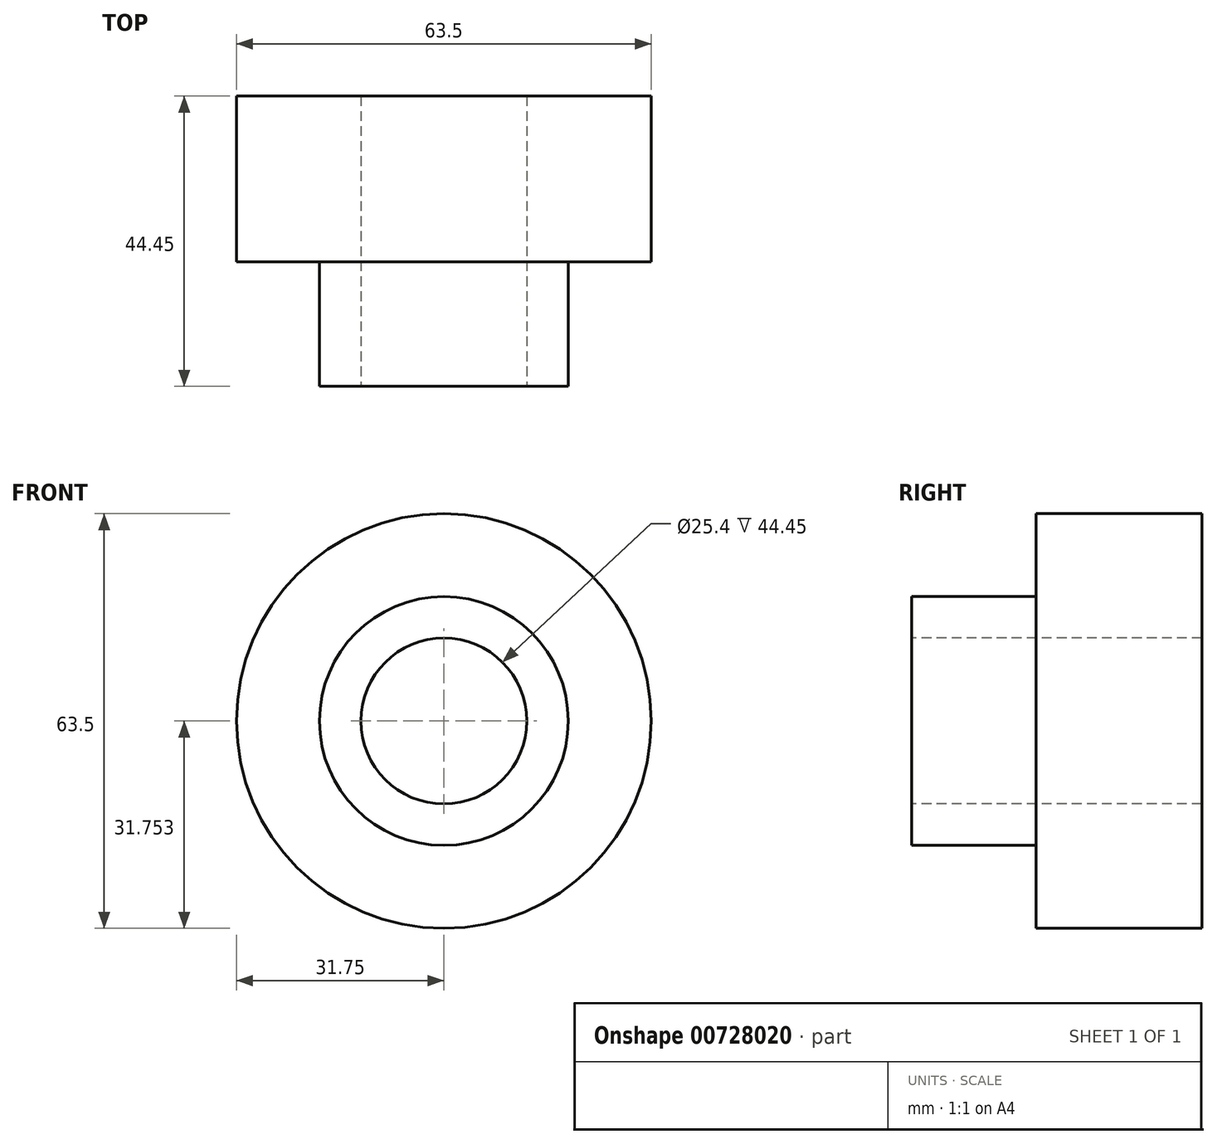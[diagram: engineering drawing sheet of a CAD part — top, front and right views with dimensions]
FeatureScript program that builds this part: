
annotation { "Feature Type Name" : "Feature", "Feature Type Description" : "" }
export const myFeature = defineFeature(function(context is Context, id is Id, definition is map)
    precondition{}
    {
        {
            var Q0;
            Q0=qCreatedBy(makeId("Front.planeOp"),FACE);
            var sketch = newSketch(context, id + "F0", { "sketchPlane" : qUnion([Q0])});
            skCircle(sketch, "E0", {"center": v(-49.89, 51.98) * mm, "radius": 31.75 * mm});
            skSolve(sketch);
        }
        {
            var Q0;
            Q0=makeQuery(id+"F0.imprint","IMPRINT",FACE,{"disambiguationData":[TD([[makeQuery(id+"F0.imprint","IMPRINT",EDGE,{"derivedFrom":sQuery(id+"F0.wireOp",EDGE,"E0")}),1.0]])]});
            extrude(context, id + "F1", {"entities" : qUnion([Q0]), "depth" : 25.4 * mm, "offsetDistance" : 25.4 * mm});
        }
        {
            var Q0;
            Q0=makeQuery(id+"F1.opExtrude","CAP_FACE",FACE,{"disambiguationData":[OSD([sQuery(id+"F0.wireOp",EDGE,"E0")])],"isStart":false});
            var sketch = newSketch(context, id + "F2", { "sketchPlane" : qUnion([Q0])});
            skCircle(sketch, "E1", {"center": v(-49.89, 51.98) * mm, "radius": 19.05 * mm});
            skSolve(sketch);
        }
        {
            var Q0;
            Q0=makeQuery(id+"F2.imprint","IMPRINT",FACE,{"disambiguationData":[TD([[makeQuery(id+"F2.imprint","IMPRINT",EDGE,{"derivedFrom":sQuery(id+"F2.wireOp",EDGE,"E1")}),1.0]])]});
            extrude(context, id + "F3", {"entities" : qUnion([Q0]), "operationType" : NewBodyOperationType.ADD, "depth" : 19.05 * mm, "offsetDistance" : 25.4 * mm});
        }
        {
            var Q0;
            Q0=makeQuery(id+"F3.opExtrude","CAP_FACE",FACE,{"disambiguationData":[OSD([sQuery(id+"F2.wireOp",EDGE,"E1")])],"isStart":false});
            var sketch = newSketch(context, id + "F4", { "sketchPlane" : qUnion([Q0])});
            skCircle(sketch, "E2", {"center": v(-49.89, 51.98) * mm, "radius": 12.7 * mm});
            skSolve(sketch);
        }
        {
            var Q0;
            Q0 = qSketchRegion(id + "F4", true);
            extrude(context, id + "F5", {"entities" : qUnion([Q0]), "operationType" : NewBodyOperationType.REMOVE, "endBound" : BoundingType.THROUGH_ALL, "oppositeDirection" : true, "depth" : 25.4 * mm, "offsetDistance" : 25.4 * mm});
        }
    });
